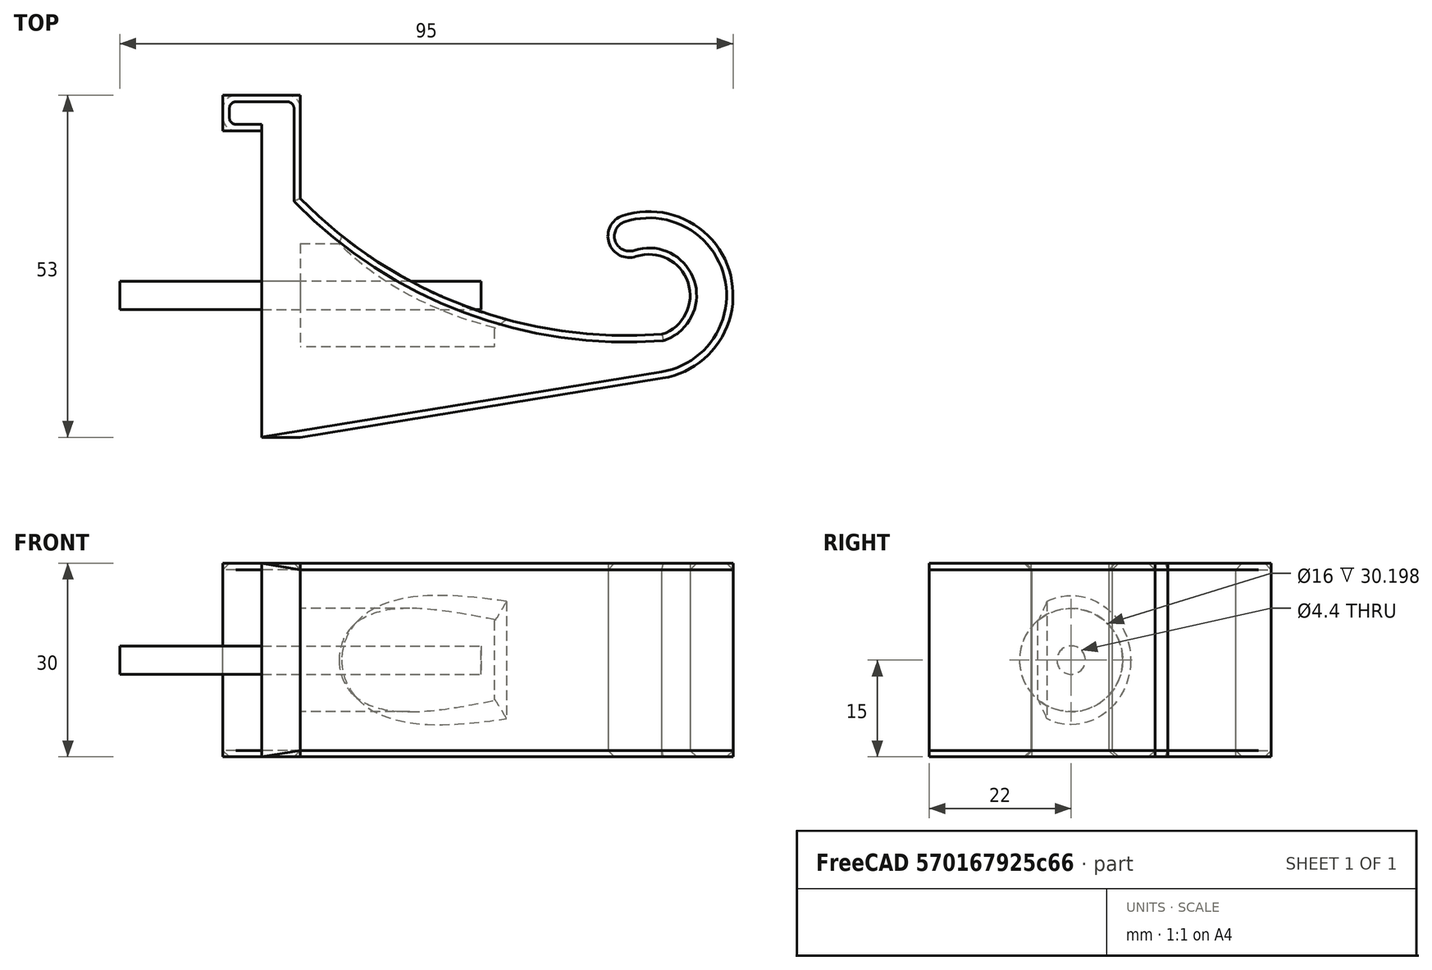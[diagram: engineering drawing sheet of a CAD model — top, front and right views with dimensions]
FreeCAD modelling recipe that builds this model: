
FCSTD DOCUMENT  (FreeCAD 0.16R)
Label: BabyGateLongShort
License: All rights reserved
LicenseURL: http://en.wikipedia.org/wiki/All_rights_reserved
objects: PartDesign::Chamfer×4, Sketcher::SketchObject×3, PartDesign::Pocket×2, PartDesign::Pad×1, PartDesign::Fillet×1, Mesh::Feature×1
note: 14 computed .brp shape members not serialized (recipe doc carries the construction recipe); baked Part::Feature solids carry a one-line shape summary decoded from their .brp

FEATURE [Sketcher::SketchObject] Sketch001
  sketch-geometry (13):
    g0: ArcOfCircle CenterX=0 CenterY=0 CenterZ=0 NormalX=0 NormalY=0 NormalZ=1 Radius=6.35 StartAngle=5.0328 EndAngle=8.1744
    g1: ArcOfCircle CenterX=0 CenterY=0 CenterZ=0 NormalX=0 NormalY=0 NormalZ=1 Radius=13 StartAngle=4.87443 EndAngle=8.1744
    g2: LineSegment StartX=2.09729 StartY=-12.8297 StartZ=0 EndX=-54 EndY=-22 EndZ=0
    g3: LineSegment StartX=-54 StartY=15 StartZ=0 EndX=-54 EndY=31 EndZ=0
    g4: LineSegment StartX=-54 StartY=31 StartZ=0 EndX=-60 EndY=31 EndZ=0
    g5: LineSegment StartX=-60 StartY=31 StartZ=0 EndX=-60 EndY=-22 EndZ=0
    g6: LineSegment StartX=-60 StartY=-22 StartZ=0 EndX=-54 EndY=-22 EndZ=0
    g7: ArcOfCircle CenterX=-3.04724 CenterY=9.18259 CenterZ=0 NormalX=0 NormalY=0 NormalZ=1 Radius=3.325 StartAngle=1.89121 EndAngle=5.0328
    g8: ArcOfCircle CenterX=-3.45392 CenterY=64.5328 CenterZ=0 NormalX=0 NormalY=0 NormalZ=1 Radius=70.7701 StartAngle=3.91687 EndAngle=4.78953
    g9: LineSegment StartX=-66 StartY=31 StartZ=0 EndX=-60 EndY=31 EndZ=0
    g10: LineSegment StartX=-60 StartY=31 StartZ=0 EndX=-60 EndY=25.5 EndZ=0
    g11: LineSegment StartX=-60 StartY=25.5 StartZ=0 EndX=-66 EndY=25.5 EndZ=0
    g12: LineSegment StartX=-66 StartY=25.5 StartZ=0 EndX=-66 EndY=31 EndZ=0
  constraints (40):
    c: Coincident(g0,g-1)
    c: Radius(g0) = 6.35
    c: DistanceX(g0,g-1) = 2
    c: Radius(g1) = 13
    c: Coincident(g1,g-1)
    c: Coincident(g2,g1)
    c: DistanceX(g3) = -54
    c: DistanceX(g2) = -54
    c: Vertical(g3)
    c: Coincident(g3,g4)
    c: Coincident(g4,g5)
    c: Vertical(g5)
    c: Coincident(g5,g6)
    c: Horizontal(g4)
    c: Horizontal(g6)
    c: DistanceX(g4,g4) = 6
    c: Tangent(g7,g1)
    c: Coincident(g7,g1)
    c: Coincident(g0,g7)
    c: Coincident(g2,g6)
    c: Tangent(g2,g1)
    c: DistanceY(g4) = 31
    c: DistanceY(g5) = -22
    c: Tangent(g0,g7)
    c: DistanceY(g3) = 15
    c: Coincident(g8,g0)
    c: Coincident(g8,g3)
    c: Angle(g8) = 0.872665
    c: Coincident(g9,g10)
    c: Coincident(g10,g11)
    c: Coincident(g11,g12)
    c: Coincident(g12,g9)
    c: Horizontal(g9)
    c: Horizontal(g11)
    c: Vertical(g10)
    c: Vertical(g12)
    c: DistanceY(g12,g12) = 5.5
    c: DistanceX(g9,g9) = 6
    c: Coincident(g9,g4)
    c: DistanceX(g0) = 2
FEATURE [PartDesign::Pad] Pad
  Length = 30
  Length2 = 100
  Sketch = -> Sketch001
  Type = 0
FEATURE [Sketcher::SketchObject] Sketch002
  Placement = pos=(-54,0,0) rot=(0.57735,0.57735,0.57735;2.0944rad)
  Support = -> Pad [Face12]
  sketch-geometry (1):
    g0: Circle CenterX=0 CenterY=15 CenterZ=0 NormalX=0 NormalY=0 NormalZ=1 Radius=2.2
  constraints (3):
    c: PointOnObject(g0,g-2)
    c: DistanceY(g-1,g0) = 15
    c: Radius(g0) = 2.2
FEATURE [PartDesign::Pocket] Pocket
  Length = 56
  Midplane = true
  Sketch = -> Sketch002
  Type = 0
FEATURE [Sketcher::SketchObject] Sketch003
  Placement = pos=(-54,0,0) rot=(0.57735,0.57735,0.57735;2.0944rad)
  Support = -> Pocket [Face2]
  sketch-geometry (1):
    g0: Circle CenterX=0 CenterY=15 CenterZ=0 NormalX=0 NormalY=0 NormalZ=1 Radius=8
  constraints (3):
    c: PointOnObject(g0,g-2)
    c: DistanceY(g0) = 15
    c: Radius(g0) = 8
FEATURE [PartDesign::Pocket] Pocket001
  Length = 30
  Reversed = true
  Sketch = -> Sketch003
  Type = 0
FEATURE [PartDesign::Fillet] Fillet
  Base = -> Pocket001 [Edge8,Edge43,Edge42]
  Radius = 2
FEATURE [PartDesign::Chamfer] Chamfer
  Base = -> Fillet [Edge34,Edge13]
  Size = 1
FEATURE [PartDesign::Chamfer] Chamfer001
  Base = -> Chamfer [Edge52,Edge14]
  Size = 1
FEATURE [PartDesign::Chamfer] Chamfer002
  Base = -> Chamfer001 [Edge22,Edge2]
  Size = 1
FEATURE [PartDesign::Chamfer] Chamfer003
  Base = -> Chamfer002 [Edge66,Edge64,Edge65]
  Size = 2
FEATURE [Mesh::Feature] Mesh  label="Chamfer003 (Meshed)"
